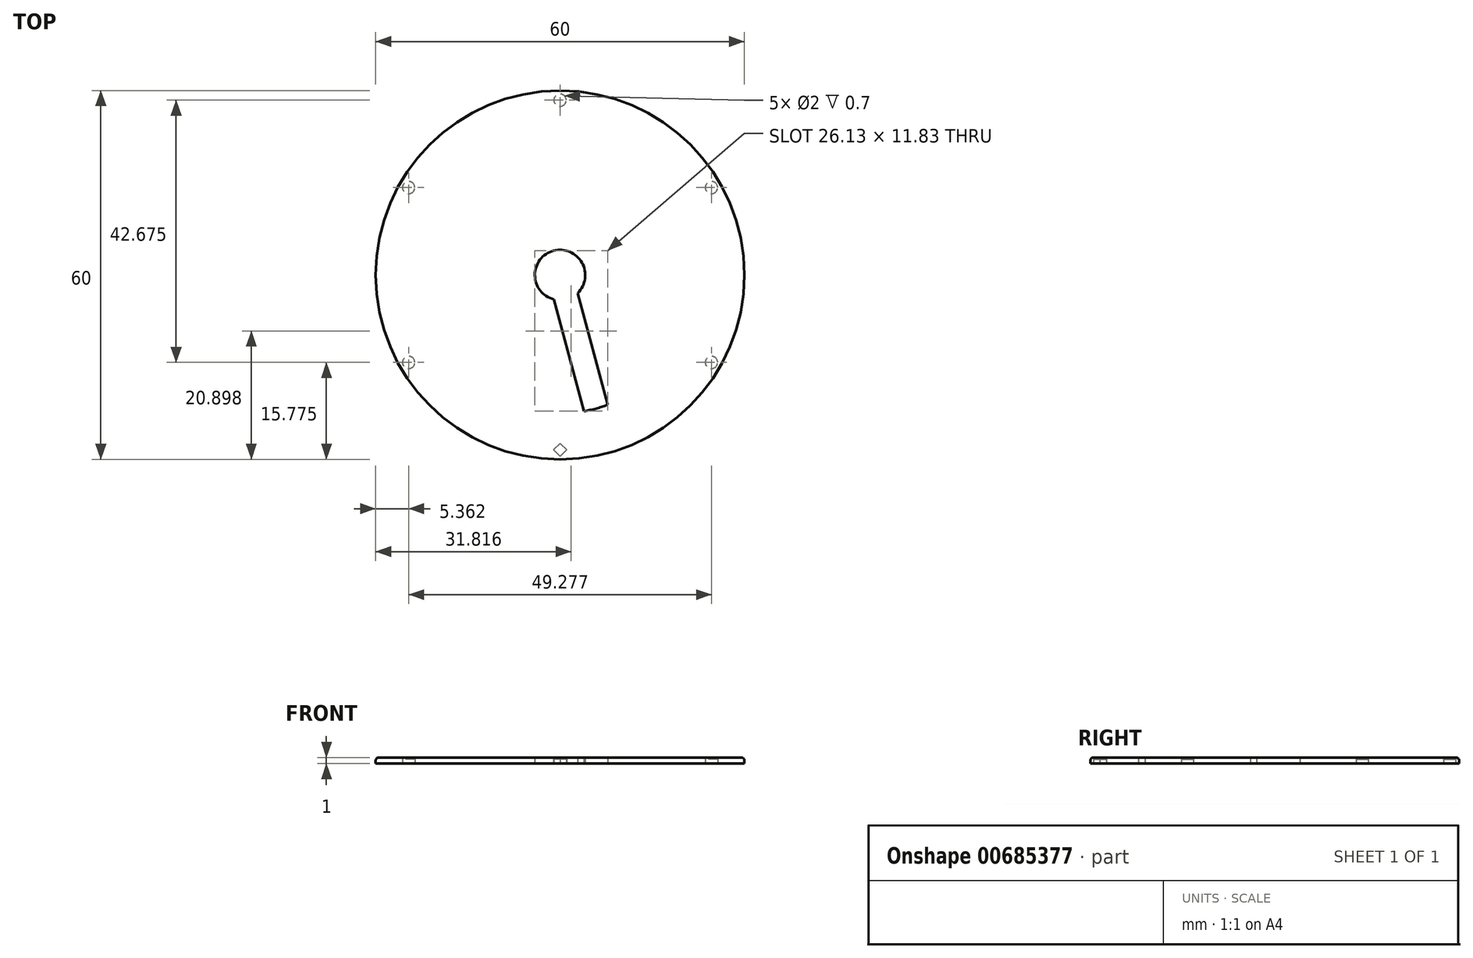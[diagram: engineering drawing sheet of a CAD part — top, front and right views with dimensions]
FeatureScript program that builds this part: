
annotation { "Feature Type Name" : "Feature", "Feature Type Description" : "" }
export const myFeature = defineFeature(function(context is Context, id is Id, definition is map)
    precondition{}
    {
        {
            var Q0;
            Q0=qCreatedBy(makeId("Top.planeOp"),FACE);
            var sketch = newSketch(context, id + "F0", { "sketchPlane" : qUnion([Q0])});
            skCircle(sketch, "E0", {"center": v(0, 0) * mm, "radius": 30 * mm});
            skCircle(sketch, "E1.0", {"center": v(0, 0) * mm, "radius": 29 * mm});
            skLineSegment(sketch, "E2.bottom", {"start": v(14.56, 26.23) * mm, "end": v(15.43, 25.73) * mm});
            skLineSegment(sketch, "E2.top", {"start": v(-15.43, -25.73) * mm, "end": v(-14.56, -26.23) * mm});
            skLineSegment(sketch, "E2.left", {"start": v(14.56, 26.23) * mm, "end": v(-15.43, -25.73) * mm});
            skLineSegment(sketch, "E2.right", {"start": v(15.43, 25.73) * mm, "end": v(-14.56, -26.23) * mm});
            skLineSegment(sketch, "E3.bottom", {"start": v(25.73, 15.43) * mm, "end": v(26.23, 14.56) * mm});
            skLineSegment(sketch, "E3.top", {"start": v(-26.23, -14.56) * mm, "end": v(-25.73, -15.43) * mm});
            skLineSegment(sketch, "E3.left", {"start": v(25.73, 15.43) * mm, "end": v(-26.23, -14.56) * mm});
            skLineSegment(sketch, "E3.right", {"start": v(26.23, 14.56) * mm, "end": v(-25.73, -15.43) * mm});
            skLineSegment(sketch, "E4", {"start": v(-38.35, 0) * mm, "end": v(39.17, 0) * mm, "construction": true});
            skLineSegment(sketch, "E5", {"start": v(0, 42.5) * mm, "end": v(0, -42.47) * mm, "construction": true});
            skLineSegment(sketch, "E6.bottom", {"start": v(-30, 0.5) * mm, "end": v(30, 0.5) * mm});
            skLineSegment(sketch, "E6.top", {"start": v(-30, -0.5) * mm, "end": v(30, -0.5) * mm});
            skLineSegment(sketch, "E6.left", {"start": v(-30, 0.5) * mm, "end": v(-30, -0.5) * mm});
            skLineSegment(sketch, "E6.right", {"start": v(30, 0.5) * mm, "end": v(30, -0.5) * mm});
            skLineSegment(sketch, "E7.bottom", {"start": v(-25.73, 15.43) * mm, "end": v(26.23, -14.56) * mm});
            skLineSegment(sketch, "E7.top", {"start": v(-26.23, 14.56) * mm, "end": v(25.73, -15.43) * mm});
            skLineSegment(sketch, "E7.left", {"start": v(-25.73, 15.43) * mm, "end": v(-26.23, 14.56) * mm});
            skLineSegment(sketch, "E7.right", {"start": v(26.23, -14.56) * mm, "end": v(25.73, -15.43) * mm});
            skLineSegment(sketch, "E8.bottom", {"start": v(-0.5, 30) * mm, "end": v(0.5, 30) * mm});
            skLineSegment(sketch, "E8.top", {"start": v(-0.5, -30) * mm, "end": v(0.5, -30) * mm});
            skLineSegment(sketch, "E8.left", {"start": v(-0.5, 30) * mm, "end": v(-0.5, -30) * mm});
            skLineSegment(sketch, "E8.right", {"start": v(0.5, 30) * mm, "end": v(0.5, -30) * mm});
            skLineSegment(sketch, "E9.bottom", {"start": v(-15.43, 25.73) * mm, "end": v(-14.56, 26.23) * mm});
            skLineSegment(sketch, "E9.top", {"start": v(14.56, -26.23) * mm, "end": v(15.43, -25.73) * mm});
            skLineSegment(sketch, "E9.left", {"start": v(-15.43, 25.73) * mm, "end": v(14.56, -26.23) * mm});
            skLineSegment(sketch, "E9.right", {"start": v(-14.56, 26.23) * mm, "end": v(15.43, -25.73) * mm});
            skCircle(sketch, "E10", {"center": v(0, 0) * mm, "radius": 13.47 * mm});
            skSolve(sketch);
        }
        {
            var Q0;
            Q0=qCreatedBy(makeId("Top.planeOp"),FACE);
            var sketch = newSketch(context, id + "F1", { "sketchPlane" : qUnion([Q0])});
            skCircle(sketch, "E11", {"center": v(0, 0) * mm, "radius": 30 * mm});
            skCircle(sketch, "E12", {"center": v(0, 0) * mm, "radius": 29 * mm});
            skSolve(sketch);
        }
        {
            var Q0;
            Q0=makeQuery(id+"F1.imprint","IMPRINT",FACE,{"disambiguationData":[TD([[makeQuery(id+"F1.imprint","IMPRINT",EDGE,{"derivedFrom":sQuery(id+"F1.wireOp",EDGE,"E11")}),1.0]])]});
            extrude(context, id + "F2", {"entities" : qUnion([Q0]), "depth" : 1 * mm, "offsetDistance" : 25 * mm});
        }
        {
            var Q0;
            Q0=makeQuery(id+"F1.imprint","IMPRINT",FACE,{"disambiguationData":[TD([[makeQuery(id+"F1.imprint","IMPRINT",EDGE,{"derivedFrom":sQuery(id+"F1.wireOp",EDGE,"E11")}),1.0]])]});
            var Q1;
            Q1=makeQuery(id+"F1.imprint","IMPRINT",FACE,{"disambiguationData":[TD([[makeQuery(id+"F1.imprint","IMPRINT",EDGE,{"derivedFrom":sQuery(id+"F1.wireOp",EDGE,"E12")}),1.0]])]});
            extrude(context, id + "F3", {"entities" : qUnion([Q0, Q1]), "operationType" : NewBodyOperationType.ADD, "depth" : 1 * mm, "offsetDistance" : 25 * mm});
        }
        {
            var Q0;
            Q0=qCreatedBy(makeId("Top.planeOp"),FACE);
            var sketch = newSketch(context, id + "F4", { "sketchPlane" : qUnion([Q0])});
            skCircle(sketch, "E13", {"center": v(0, 0) * mm, "radius": 28.45 * mm});
            skLineSegment(sketch, "E14", {"start": v(0, 28.45) * mm, "end": v(0, -28.45) * mm, "construction": true});
            skLineSegment(sketch, "E15", {"start": v(24.64, 14.22) * mm, "end": v(0, 0) * mm, "construction": true});
            skLineSegment(sketch, "E16", {"start": v(14.23, 24.64) * mm, "end": v(0, 0) * mm, "construction": true});
            skLineSegment(sketch, "E17", {"start": v(0, 0) * mm, "end": v(28.45, 0) * mm, "construction": true});
            skLineSegment(sketch, "E18", {"start": v(0, 0) * mm, "end": v(24.64, -14.22) * mm, "construction": true});
            skLineSegment(sketch, "E19", {"start": v(0, 0) * mm, "end": v(14.23, -24.64) * mm, "construction": true});
            skLineSegment(sketch, "E20", {"start": v(0, 0) * mm, "end": v(-14.23, 24.64) * mm, "construction": true});
            skLineSegment(sketch, "E21", {"start": v(0, 0) * mm, "end": v(-24.64, 14.22) * mm, "construction": true});
            skLineSegment(sketch, "E22", {"start": v(0, 0) * mm, "end": v(-28.45, 0) * mm, "construction": true});
            skLineSegment(sketch, "E23", {"start": v(0, 0) * mm, "end": v(-24.64, -14.23) * mm, "construction": true});
            skLineSegment(sketch, "E24", {"start": v(0, 0) * mm, "end": v(-14.22, -24.64) * mm, "construction": true});
            skCircle(sketch, "E25", {"center": v(0, 28.45) * mm, "radius": 1.5 * mm});
            skCircle(sketch, "E26", {"center": v(24.64, 14.22) * mm, "radius": 1.5 * mm});
            skCircle(sketch, "E27", {"center": v(24.64, -14.22) * mm, "radius": 1.5 * mm});
            skCircle(sketch, "E28", {"center": v(0, -28.45) * mm, "radius": 1.5 * mm});
            skCircle(sketch, "E29", {"center": v(-24.64, -14.23) * mm, "radius": 1.5 * mm});
            skCircle(sketch, "E30", {"center": v(-24.64, 14.22) * mm, "radius": 1.5 * mm});
            skCircle(sketch, "E31", {"center": v(-24.64, 14.22) * mm, "radius": 1 * mm});
            skCircle(sketch, "E32", {"center": v(0, 28.45) * mm, "radius": 1 * mm});
            skCircle(sketch, "E33", {"center": v(24.64, 14.22) * mm, "radius": 1 * mm});
            skCircle(sketch, "E34", {"center": v(24.64, -14.22) * mm, "radius": 1 * mm});
            skCircle(sketch, "E35", {"center": v(-24.64, -14.23) * mm, "radius": 1 * mm});
            skLineSegment(sketch, "E36.bottom", {"start": v(1.06, -28.45) * mm, "end": v(0, -29.51) * mm});
            skLineSegment(sketch, "E36.top", {"start": v(0, -27.39) * mm, "end": v(-1.06, -28.45) * mm});
            skLineSegment(sketch, "E36.left", {"start": v(1.06, -28.45) * mm, "end": v(0, -27.39) * mm});
            skLineSegment(sketch, "E36.right", {"start": v(0, -29.51) * mm, "end": v(-1.06, -28.45) * mm});
            skSolve(sketch);
        }
        {
            var Q0;
            {var subQ0=sQuery(id+"F4.wireOp",EDGE,"E30");var subQ1=sQuery(id+"F4.wireOp",EDGE,"E13");var subQ2=makeQuery(id+"F4.imprint","INTERSECT",VERTEX,{"disambiguationData":[OD(0.0)],"derivedFrom":[subQ1,subQ0]});Q0=makeQuery(id+"F4.imprint","IMPRINT",FACE,{"disambiguationData":[TD([[makeQuery(id+"F4.imprint","IMPRINT",EDGE,{"disambiguationData":[TD([[subQ2,-1.0]])],"derivedFrom":subQ1}),1.0]])]});}
            var Q1;
            {var subQ0=sQuery(id+"F4.wireOp",EDGE,"E30");var subQ1=sQuery(id+"F4.wireOp",EDGE,"E13");var subQ2=makeQuery(id+"F4.imprint","INTERSECT",VERTEX,{"disambiguationData":[OD(0.0)],"derivedFrom":[subQ1,subQ0]});Q1=makeQuery(id+"F4.imprint","IMPRINT",FACE,{"disambiguationData":[TD([[makeQuery(id+"F4.imprint","IMPRINT",EDGE,{"disambiguationData":[TD([[subQ2,-1.0]])],"derivedFrom":subQ1}),-1.0]])]});}
            var Q2;
            {var subQ0=sQuery(id+"F4.wireOp",EDGE,"E25");var subQ1=sQuery(id+"F4.wireOp",EDGE,"E13");var subQ2=makeQuery(id+"F4.imprint","INTERSECT",VERTEX,{"disambiguationData":[OD(0.0)],"derivedFrom":[subQ1,subQ0]});Q2=makeQuery(id+"F4.imprint","IMPRINT",FACE,{"disambiguationData":[TD([[makeQuery(id+"F4.imprint","IMPRINT",EDGE,{"disambiguationData":[TD([[subQ2,-1.0]])],"derivedFrom":subQ1}),1.0]])]});}
            var Q3;
            {var subQ0=sQuery(id+"F4.wireOp",EDGE,"E25");var subQ1=sQuery(id+"F4.wireOp",EDGE,"E13");var subQ2=makeQuery(id+"F4.imprint","INTERSECT",VERTEX,{"disambiguationData":[OD(0.0)],"derivedFrom":[subQ1,subQ0]});Q3=makeQuery(id+"F4.imprint","IMPRINT",FACE,{"disambiguationData":[TD([[makeQuery(id+"F4.imprint","IMPRINT",EDGE,{"disambiguationData":[TD([[subQ2,-1.0]])],"derivedFrom":subQ1}),-1.0]])]});}
            var Q4;
            {var subQ0=sQuery(id+"F4.wireOp",EDGE,"E26");var subQ1=sQuery(id+"F4.wireOp",EDGE,"E13");var subQ2=makeQuery(id+"F4.imprint","INTERSECT",VERTEX,{"disambiguationData":[OD(0.0)],"derivedFrom":[subQ1,subQ0]});Q4=makeQuery(id+"F4.imprint","IMPRINT",FACE,{"disambiguationData":[TD([[makeQuery(id+"F4.imprint","IMPRINT",EDGE,{"disambiguationData":[TD([[subQ2,-1.0]])],"derivedFrom":subQ1}),-1.0]])]});}
            var Q5;
            {var subQ0=sQuery(id+"F4.wireOp",EDGE,"E26");var subQ1=sQuery(id+"F4.wireOp",EDGE,"E13");var subQ2=makeQuery(id+"F4.imprint","INTERSECT",VERTEX,{"disambiguationData":[OD(0.0)],"derivedFrom":[subQ1,subQ0]});Q5=makeQuery(id+"F4.imprint","IMPRINT",FACE,{"disambiguationData":[TD([[makeQuery(id+"F4.imprint","IMPRINT",EDGE,{"disambiguationData":[TD([[subQ2,-1.0]])],"derivedFrom":subQ1}),1.0]])]});}
            var Q6;
            {var subQ0=sQuery(id+"F4.wireOp",EDGE,"E29");var subQ1=sQuery(id+"F4.wireOp",EDGE,"E13");var subQ2=makeQuery(id+"F4.imprint","INTERSECT",VERTEX,{"disambiguationData":[OD(0.0)],"derivedFrom":[subQ1,subQ0]});Q6=makeQuery(id+"F4.imprint","IMPRINT",FACE,{"disambiguationData":[TD([[makeQuery(id+"F4.imprint","IMPRINT",EDGE,{"disambiguationData":[TD([[subQ2,-1.0]])],"derivedFrom":subQ1}),1.0]])]});}
            var Q7;
            {var subQ0=sQuery(id+"F4.wireOp",EDGE,"E29");var subQ1=sQuery(id+"F4.wireOp",EDGE,"E13");var subQ2=makeQuery(id+"F4.imprint","INTERSECT",VERTEX,{"disambiguationData":[OD(0.0)],"derivedFrom":[subQ1,subQ0]});Q7=makeQuery(id+"F4.imprint","IMPRINT",FACE,{"disambiguationData":[TD([[makeQuery(id+"F4.imprint","IMPRINT",EDGE,{"disambiguationData":[TD([[subQ2,-1.0]])],"derivedFrom":subQ1}),-1.0]])]});}
            var Q8;
            {var subQ3=sQuery(id+"F4.wireOp",EDGE,"E13");var subQ5=sQuery(id+"F4.wireOp",EDGE,"E28");var subQ6=makeQuery(id+"F4.imprint","INTERSECT",VERTEX,{"disambiguationData":[OD(0.0)],"derivedFrom":[subQ3,subQ5]});Q8=makeQuery(id+"F4.imprint","IMPRINT",FACE,{"disambiguationData":[TD([[makeQuery(id+"F4.imprint","IMPRINT",EDGE,{"disambiguationData":[TD([[subQ6,-1.0]])],"derivedFrom":subQ3}),1.0]])]});}
            var Q9;
            {var subQ6=sQuery(id+"F4.wireOp",EDGE,"E36.bottom");Q9=makeQuery(id+"F4.imprint","IMPRINT",FACE,{"disambiguationData":[TD([[makeQuery(id+"F4.imprint","IMPRINT",EDGE,{"derivedFrom":subQ6}),1.0]])]});}
            var Q10;
            {var subQ0=sQuery(id+"F4.wireOp",EDGE,"E27");var subQ1=sQuery(id+"F4.wireOp",EDGE,"E13");var subQ2=makeQuery(id+"F4.imprint","INTERSECT",VERTEX,{"disambiguationData":[OD(0.0)],"derivedFrom":[subQ1,subQ0]});Q10=makeQuery(id+"F4.imprint","IMPRINT",FACE,{"disambiguationData":[TD([[makeQuery(id+"F4.imprint","IMPRINT",EDGE,{"disambiguationData":[TD([[subQ2,-1.0]])],"derivedFrom":subQ1}),-1.0]])]});}
            var Q11;
            {var subQ0=sQuery(id+"F4.wireOp",EDGE,"E27");var subQ1=sQuery(id+"F4.wireOp",EDGE,"E13");var subQ2=makeQuery(id+"F4.imprint","INTERSECT",VERTEX,{"disambiguationData":[OD(0.0)],"derivedFrom":[subQ1,subQ0]});Q11=makeQuery(id+"F4.imprint","IMPRINT",FACE,{"disambiguationData":[TD([[makeQuery(id+"F4.imprint","IMPRINT",EDGE,{"disambiguationData":[TD([[subQ2,-1.0]])],"derivedFrom":subQ1}),1.0]])]});}
            var Q12;
            {var subQ0=sQuery(id+"F4.wireOp",EDGE,"E31");var subQ1=sQuery(id+"F4.wireOp",EDGE,"E13");var subQ2=makeQuery(id+"F4.imprint","INTERSECT",VERTEX,{"disambiguationData":[OD(0.0)],"derivedFrom":[subQ1,subQ0]});Q12=makeQuery(id+"F4.imprint","IMPRINT",FACE,{"disambiguationData":[TD([[makeQuery(id+"F4.imprint","IMPRINT",EDGE,{"disambiguationData":[TD([[subQ2,-1.0]])],"derivedFrom":subQ1}),1.0]])]});}
            var Q13;
            {var subQ0=sQuery(id+"F4.wireOp",EDGE,"E31");var subQ1=sQuery(id+"F4.wireOp",EDGE,"E13");var subQ2=makeQuery(id+"F4.imprint","INTERSECT",VERTEX,{"disambiguationData":[OD(0.0)],"derivedFrom":[subQ1,subQ0]});Q13=makeQuery(id+"F4.imprint","IMPRINT",FACE,{"disambiguationData":[TD([[makeQuery(id+"F4.imprint","IMPRINT",EDGE,{"disambiguationData":[TD([[subQ2,-1.0]])],"derivedFrom":subQ1}),-1.0]])]});}
            var Q14;
            {var subQ0=sQuery(id+"F4.wireOp",EDGE,"E32");var subQ1=sQuery(id+"F4.wireOp",EDGE,"E13");var subQ2=makeQuery(id+"F4.imprint","INTERSECT",VERTEX,{"disambiguationData":[OD(0.0)],"derivedFrom":[subQ1,subQ0]});Q14=makeQuery(id+"F4.imprint","IMPRINT",FACE,{"disambiguationData":[TD([[makeQuery(id+"F4.imprint","IMPRINT",EDGE,{"disambiguationData":[TD([[subQ2,-1.0]])],"derivedFrom":subQ1}),-1.0]])]});}
            var Q15;
            {var subQ0=sQuery(id+"F4.wireOp",EDGE,"E32");var subQ1=sQuery(id+"F4.wireOp",EDGE,"E13");var subQ2=makeQuery(id+"F4.imprint","INTERSECT",VERTEX,{"disambiguationData":[OD(0.0)],"derivedFrom":[subQ1,subQ0]});Q15=makeQuery(id+"F4.imprint","IMPRINT",FACE,{"disambiguationData":[TD([[makeQuery(id+"F4.imprint","IMPRINT",EDGE,{"disambiguationData":[TD([[subQ2,-1.0]])],"derivedFrom":subQ1}),1.0]])]});}
            var Q16;
            {var subQ0=sQuery(id+"F4.wireOp",EDGE,"E33");var subQ1=sQuery(id+"F4.wireOp",EDGE,"E13");var subQ2=makeQuery(id+"F4.imprint","INTERSECT",VERTEX,{"disambiguationData":[OD(0.0)],"derivedFrom":[subQ1,subQ0]});Q16=makeQuery(id+"F4.imprint","IMPRINT",FACE,{"disambiguationData":[TD([[makeQuery(id+"F4.imprint","IMPRINT",EDGE,{"disambiguationData":[TD([[subQ2,-1.0]])],"derivedFrom":subQ1}),-1.0]])]});}
            var Q17;
            {var subQ0=sQuery(id+"F4.wireOp",EDGE,"E33");var subQ1=sQuery(id+"F4.wireOp",EDGE,"E13");var subQ2=makeQuery(id+"F4.imprint","INTERSECT",VERTEX,{"disambiguationData":[OD(0.0)],"derivedFrom":[subQ1,subQ0]});Q17=makeQuery(id+"F4.imprint","IMPRINT",FACE,{"disambiguationData":[TD([[makeQuery(id+"F4.imprint","IMPRINT",EDGE,{"disambiguationData":[TD([[subQ2,-1.0]])],"derivedFrom":subQ1}),1.0]])]});}
            var Q18;
            {var subQ0=sQuery(id+"F4.wireOp",EDGE,"E34");var subQ1=sQuery(id+"F4.wireOp",EDGE,"E13");var subQ2=makeQuery(id+"F4.imprint","INTERSECT",VERTEX,{"disambiguationData":[OD(0.0)],"derivedFrom":[subQ1,subQ0]});Q18=makeQuery(id+"F4.imprint","IMPRINT",FACE,{"disambiguationData":[TD([[makeQuery(id+"F4.imprint","IMPRINT",EDGE,{"disambiguationData":[TD([[subQ2,-1.0]])],"derivedFrom":subQ1}),-1.0]])]});}
            var Q19;
            {var subQ0=sQuery(id+"F4.wireOp",EDGE,"E34");var subQ1=sQuery(id+"F4.wireOp",EDGE,"E13");var subQ2=makeQuery(id+"F4.imprint","INTERSECT",VERTEX,{"disambiguationData":[OD(0.0)],"derivedFrom":[subQ1,subQ0]});Q19=makeQuery(id+"F4.imprint","IMPRINT",FACE,{"disambiguationData":[TD([[makeQuery(id+"F4.imprint","IMPRINT",EDGE,{"disambiguationData":[TD([[subQ2,-1.0]])],"derivedFrom":subQ1}),1.0]])]});}
            var Q20;
            {var subQ1=sQuery(id+"F4.wireOp",EDGE,"E36.bottom");Q20=makeQuery(id+"F4.imprint","IMPRINT",FACE,{"disambiguationData":[TD([[makeQuery(id+"F4.imprint","IMPRINT",EDGE,{"derivedFrom":subQ1}),-1.0]])]});}
            var Q21;
            {var subQ0=sQuery(id+"F4.wireOp",EDGE,"E35");var subQ1=sQuery(id+"F4.wireOp",EDGE,"E13");var subQ2=makeQuery(id+"F4.imprint","INTERSECT",VERTEX,{"disambiguationData":[OD(0.0)],"derivedFrom":[subQ1,subQ0]});Q21=makeQuery(id+"F4.imprint","IMPRINT",FACE,{"disambiguationData":[TD([[makeQuery(id+"F4.imprint","IMPRINT",EDGE,{"disambiguationData":[TD([[subQ2,-1.0]])],"derivedFrom":subQ1}),-1.0]])]});}
            var Q22;
            {var subQ0=sQuery(id+"F4.wireOp",EDGE,"E35");var subQ1=sQuery(id+"F4.wireOp",EDGE,"E13");var subQ2=makeQuery(id+"F4.imprint","INTERSECT",VERTEX,{"disambiguationData":[OD(0.0)],"derivedFrom":[subQ1,subQ0]});Q22=makeQuery(id+"F4.imprint","IMPRINT",FACE,{"disambiguationData":[TD([[makeQuery(id+"F4.imprint","IMPRINT",EDGE,{"disambiguationData":[TD([[subQ2,-1.0]])],"derivedFrom":subQ1}),1.0]])]});}
            var Q23;
            {var subQ0=sQuery(id+"F4.wireOp",EDGE,"E36.top");var subQ1=sQuery(id+"F4.wireOp",EDGE,"E13");var subQ2=makeQuery(id+"F4.imprint","INTERSECT",VERTEX,{"derivedFrom":[subQ1,subQ0]});Q23=makeQuery(id+"F4.imprint","IMPRINT",FACE,{"disambiguationData":[TD([[makeQuery(id+"F4.imprint","IMPRINT",EDGE,{"disambiguationData":[TD([[subQ2,-1.0]])],"derivedFrom":subQ1}),1.0]])]});}
            extrude(context, id + "F5", {"entities" : qUnion([Q0, Q1, Q2, Q3, Q4, Q5, Q6, Q7, Q8, Q9, Q10, Q11, Q12, Q13, Q14, Q15, Q16, Q17, Q18, Q19, Q20, Q21, Q22, Q23]), "operationType" : NewBodyOperationType.ADD, "depth" : 1 * mm, "offsetDistance" : 25 * mm});
        }
        {
            var Q0;
            {var subQ0=sQuery(id+"F4.wireOp",EDGE,"E31");var subQ1=sQuery(id+"F4.wireOp",EDGE,"E13");var subQ2=makeQuery(id+"F4.imprint","INTERSECT",VERTEX,{"disambiguationData":[OD(0.0)],"derivedFrom":[subQ1,subQ0]});Q0=makeQuery(id+"F4.imprint","IMPRINT",FACE,{"disambiguationData":[TD([[makeQuery(id+"F4.imprint","IMPRINT",EDGE,{"disambiguationData":[TD([[subQ2,-1.0]])],"derivedFrom":subQ1}),-1.0]])]});}
            var Q1;
            {var subQ0=sQuery(id+"F4.wireOp",EDGE,"E31");var subQ1=sQuery(id+"F4.wireOp",EDGE,"E13");var subQ2=makeQuery(id+"F4.imprint","INTERSECT",VERTEX,{"disambiguationData":[OD(0.0)],"derivedFrom":[subQ1,subQ0]});Q1=makeQuery(id+"F4.imprint","IMPRINT",FACE,{"disambiguationData":[TD([[makeQuery(id+"F4.imprint","IMPRINT",EDGE,{"disambiguationData":[TD([[subQ2,-1.0]])],"derivedFrom":subQ1}),1.0]])]});}
            var Q2;
            {var subQ0=sQuery(id+"F4.wireOp",EDGE,"E32");var subQ1=sQuery(id+"F4.wireOp",EDGE,"E13");var subQ2=makeQuery(id+"F4.imprint","INTERSECT",VERTEX,{"disambiguationData":[OD(0.0)],"derivedFrom":[subQ1,subQ0]});Q2=makeQuery(id+"F4.imprint","IMPRINT",FACE,{"disambiguationData":[TD([[makeQuery(id+"F4.imprint","IMPRINT",EDGE,{"disambiguationData":[TD([[subQ2,-1.0]])],"derivedFrom":subQ1}),-1.0]])]});}
            var Q3;
            {var subQ0=sQuery(id+"F4.wireOp",EDGE,"E32");var subQ1=sQuery(id+"F4.wireOp",EDGE,"E13");var subQ2=makeQuery(id+"F4.imprint","INTERSECT",VERTEX,{"disambiguationData":[OD(0.0)],"derivedFrom":[subQ1,subQ0]});Q3=makeQuery(id+"F4.imprint","IMPRINT",FACE,{"disambiguationData":[TD([[makeQuery(id+"F4.imprint","IMPRINT",EDGE,{"disambiguationData":[TD([[subQ2,-1.0]])],"derivedFrom":subQ1}),1.0]])]});}
            var Q4;
            {var subQ0=sQuery(id+"F4.wireOp",EDGE,"E33");var subQ1=sQuery(id+"F4.wireOp",EDGE,"E13");var subQ2=makeQuery(id+"F4.imprint","INTERSECT",VERTEX,{"disambiguationData":[OD(0.0)],"derivedFrom":[subQ1,subQ0]});Q4=makeQuery(id+"F4.imprint","IMPRINT",FACE,{"disambiguationData":[TD([[makeQuery(id+"F4.imprint","IMPRINT",EDGE,{"disambiguationData":[TD([[subQ2,-1.0]])],"derivedFrom":subQ1}),1.0]])]});}
            var Q5;
            {var subQ0=sQuery(id+"F4.wireOp",EDGE,"E33");var subQ1=sQuery(id+"F4.wireOp",EDGE,"E13");var subQ2=makeQuery(id+"F4.imprint","INTERSECT",VERTEX,{"disambiguationData":[OD(0.0)],"derivedFrom":[subQ1,subQ0]});Q5=makeQuery(id+"F4.imprint","IMPRINT",FACE,{"disambiguationData":[TD([[makeQuery(id+"F4.imprint","IMPRINT",EDGE,{"disambiguationData":[TD([[subQ2,-1.0]])],"derivedFrom":subQ1}),-1.0]])]});}
            var Q6;
            {var subQ0=sQuery(id+"F4.wireOp",EDGE,"E34");var subQ1=sQuery(id+"F4.wireOp",EDGE,"E13");var subQ2=makeQuery(id+"F4.imprint","INTERSECT",VERTEX,{"disambiguationData":[OD(0.0)],"derivedFrom":[subQ1,subQ0]});Q6=makeQuery(id+"F4.imprint","IMPRINT",FACE,{"disambiguationData":[TD([[makeQuery(id+"F4.imprint","IMPRINT",EDGE,{"disambiguationData":[TD([[subQ2,-1.0]])],"derivedFrom":subQ1}),1.0]])]});}
            var Q7;
            {var subQ0=sQuery(id+"F4.wireOp",EDGE,"E34");var subQ1=sQuery(id+"F4.wireOp",EDGE,"E13");var subQ2=makeQuery(id+"F4.imprint","INTERSECT",VERTEX,{"disambiguationData":[OD(0.0)],"derivedFrom":[subQ1,subQ0]});Q7=makeQuery(id+"F4.imprint","IMPRINT",FACE,{"disambiguationData":[TD([[makeQuery(id+"F4.imprint","IMPRINT",EDGE,{"disambiguationData":[TD([[subQ2,-1.0]])],"derivedFrom":subQ1}),-1.0]])]});}
            var Q8;
            {var subQ1=sQuery(id+"F4.wireOp",EDGE,"E36.bottom");Q8=makeQuery(id+"F4.imprint","IMPRINT",FACE,{"disambiguationData":[TD([[makeQuery(id+"F4.imprint","IMPRINT",EDGE,{"derivedFrom":subQ1}),-1.0]])]});}
            var Q9;
            {var subQ0=sQuery(id+"F4.wireOp",EDGE,"E36.top");var subQ1=sQuery(id+"F4.wireOp",EDGE,"E13");var subQ2=makeQuery(id+"F4.imprint","INTERSECT",VERTEX,{"derivedFrom":[subQ1,subQ0]});Q9=makeQuery(id+"F4.imprint","IMPRINT",FACE,{"disambiguationData":[TD([[makeQuery(id+"F4.imprint","IMPRINT",EDGE,{"disambiguationData":[TD([[subQ2,-1.0]])],"derivedFrom":subQ1}),1.0]])]});}
            var Q10;
            {var subQ0=sQuery(id+"F4.wireOp",EDGE,"E35");var subQ1=sQuery(id+"F4.wireOp",EDGE,"E13");var subQ2=makeQuery(id+"F4.imprint","INTERSECT",VERTEX,{"disambiguationData":[OD(0.0)],"derivedFrom":[subQ1,subQ0]});Q10=makeQuery(id+"F4.imprint","IMPRINT",FACE,{"disambiguationData":[TD([[makeQuery(id+"F4.imprint","IMPRINT",EDGE,{"disambiguationData":[TD([[subQ2,-1.0]])],"derivedFrom":subQ1}),-1.0]])]});}
            var Q11;
            {var subQ0=sQuery(id+"F4.wireOp",EDGE,"E35");var subQ1=sQuery(id+"F4.wireOp",EDGE,"E13");var subQ2=makeQuery(id+"F4.imprint","INTERSECT",VERTEX,{"disambiguationData":[OD(0.0)],"derivedFrom":[subQ1,subQ0]});Q11=makeQuery(id+"F4.imprint","IMPRINT",FACE,{"disambiguationData":[TD([[makeQuery(id+"F4.imprint","IMPRINT",EDGE,{"disambiguationData":[TD([[subQ2,-1.0]])],"derivedFrom":subQ1}),1.0]])]});}
            extrude(context, id + "F6", {"entities" : qUnion([Q0, Q1, Q2, Q3, Q4, Q5, Q6, Q7, Q8, Q9, Q10, Q11]), "operationType" : NewBodyOperationType.REMOVE, "depth" : .7 * mm, "offsetDistance" : 25 * mm});
        }
        {
            var Q0;
            Q0=qCreatedBy(makeId("Top.planeOp"),FACE);
            var sketch = newSketch(context, id + "F7", { "sketchPlane" : qUnion([Q0])});
            skCircle(sketch, "E37", {"center": v(0, 0) * mm, "radius": 4.1 * mm});
            skLineSegment(sketch, "E38", {"start": v(0, 0) * mm, "end": v(7.76, -28.98) * mm});
            skLineSegment(sketch, "E39.0", {"start": v(-1.93, -0.52) * mm, "end": v(5.91, -29.8) * mm});
            skLineSegment(sketch, "E40.0", {"start": v(1.93, 0.52) * mm, "end": v(9.8, -28.83) * mm});
            skCircle(sketch, "E41", {"center": v(0, 0) * mm, "radius": 22.5 * mm});
            skSolve(sketch);
        }
        {
            var Q0;
            {var subQ0=sQuery(id+"F7.wireOp",EDGE,"E37");var subQ1=makeQuery(id+"F7.imprint","INTERSECT",VERTEX,{"derivedFrom":[subQ0,sQuery(id+"F7.wireOp",EDGE,"E39.0")]});Q0=makeQuery(id+"F7.imprint","IMPRINT",FACE,{"disambiguationData":[TD([[makeQuery(id+"F7.imprint","IMPRINT",EDGE,{"disambiguationData":[TD([[subQ1,-1.0]])],"derivedFrom":subQ0}),1.0]])]});}
            var Q1;
            {var subQ0=sQuery(id+"F7.wireOp",EDGE,"E39.0");var subQ1=sQuery(id+"F7.wireOp",EDGE,"E37");var subQ2=makeQuery(id+"F7.imprint","INTERSECT",VERTEX,{"derivedFrom":[subQ1,subQ0]});Q1=makeQuery(id+"F7.imprint","IMPRINT",FACE,{"disambiguationData":[TD([[makeQuery(id+"F7.imprint","IMPRINT",EDGE,{"disambiguationData":[TD([[subQ2,-1.0]])],"derivedFrom":subQ1}),-1.0]])]});}
            var Q2;
            {var subQ0=sQuery(id+"F7.wireOp",EDGE,"E40.0");var subQ1=sQuery(id+"F7.wireOp",EDGE,"E37");var subQ2=makeQuery(id+"F7.imprint","INTERSECT",VERTEX,{"derivedFrom":[subQ1,subQ0]});Q2=makeQuery(id+"F7.imprint","IMPRINT",FACE,{"disambiguationData":[TD([[makeQuery(id+"F7.imprint","IMPRINT",EDGE,{"disambiguationData":[TD([[subQ2,1.0]])],"derivedFrom":subQ1}),-1.0]])]});}
            var Q3;
            {var subQ0=sQuery(id+"F7.wireOp",EDGE,"hZQpLc18-hGwi-RvbU-mkqQ-O1lpG7E0jyzC");var subQ1=sQuery(id+"F7.wireOp",EDGE,"E38");var subQ2=makeQuery(id+"F7.imprint","INTERSECT",VERTEX,{"disambiguationData":[OD(0.0)],"derivedFrom":[subQ1,subQ0]});Q3=makeQuery(id+"F7.imprint","IMPRINT",FACE,{"disambiguationData":[TD([[makeQuery(id+"F7.imprint","IMPRINT",EDGE,{"disambiguationData":[TD([[subQ2,1.0]])],"derivedFrom":subQ1}),1.0]])]});}
            var Q4;
            {var subQ0=sQuery(id+"F7.wireOp",EDGE,"hZQpLc18-hGwi-RvbU-mkqQ-O1lpG7E0jyzC");var subQ1=sQuery(id+"F7.wireOp",EDGE,"E38");var subQ2=makeQuery(id+"F7.imprint","INTERSECT",VERTEX,{"disambiguationData":[OD(0.0)],"derivedFrom":[subQ1,subQ0]});Q4=makeQuery(id+"F7.imprint","IMPRINT",FACE,{"disambiguationData":[TD([[makeQuery(id+"F7.imprint","IMPRINT",EDGE,{"disambiguationData":[TD([[subQ2,1.0]])],"derivedFrom":subQ1}),-1.0]])]});}
            extrude(context, id + "F8", {"entities" : qUnion([Q0, Q1, Q2, Q3, Q4]), "operationType" : NewBodyOperationType.REMOVE, "depth" : 1 * mm, "offsetDistance" : 25 * mm});
        }
        {
            var Q0;
            {var subQ0=sQuery(id+"F4.wireOp",EDGE,"E28");var subQ1=sQuery(id+"F4.wireOp",EDGE,"E27");var subQ2=sQuery(id+"F1.wireOp",EDGE,"E11");Q0=makeQuery(id+"F5.boolean.opBoolean","SPLIT",EDGE,{"disambiguationData":[TD([makeQuery(id+"F2.opExtrude","SWEPT_FACE",FACE,{"disambiguationData":[OSD([subQ2])]}),makeQuery(id+"F2.opExtrude","CAP_FACE",FACE,{"disambiguationData":[OSD([subQ2,sQuery(id+"F1.wireOp",EDGE,"E12")])],"isStart":false}),makeQuery(id+"F3.opExtrude","CAP_FACE",FACE,{"disambiguationData":[OSD([subQ2])],"isStart":false}),makeQuery(id+"F5.opExtrude","CAP_FACE",FACE,{"disambiguationData":[OSD([sQuery(id+"F4.wireOp",EDGE,"E25")])],"isStart":false}),makeQuery(id+"F5.opExtrude","CAP_FACE",FACE,{"disambiguationData":[OSD([sQuery(id+"F4.wireOp",EDGE,"E26")])],"isStart":false}),makeQuery(id+"F5.opExtrude","SWEPT_FACE",FACE,{"disambiguationData":[OSD([subQ1])]}),makeQuery(id+"F5.opExtrude","CAP_FACE",FACE,{"disambiguationData":[OSD([subQ1])],"isStart":false}),makeQuery(id+"F5.opExtrude","SWEPT_FACE",FACE,{"disambiguationData":[OSD([subQ0])]}),makeQuery(id+"F5.opExtrude","CAP_FACE",FACE,{"disambiguationData":[OSD([subQ0])],"isStart":false}),makeQuery(id+"F5.opExtrude","CAP_FACE",FACE,{"disambiguationData":[OSD([sQuery(id+"F4.wireOp",EDGE,"E29")])],"isStart":false}),makeQuery(id+"F5.opExtrude","CAP_FACE",FACE,{"disambiguationData":[OSD([sQuery(id+"F4.wireOp",EDGE,"E30")])],"isStart":false})])],"derivedFrom":makeQuery(id+"F2.opExtrude","CAP_EDGE",EDGE,{"disambiguationData":[OSD([subQ2])],"isStart":false})});}
            var Q1;
            Q1=makeQuery(id+"F8.boolean.opBoolean","COPY",EDGE,{"derivedFrom":makeQuery(id+"F8.opExtrude","CAP_EDGE",EDGE,{"disambiguationData":[OSD([sQuery(id+"F7.wireOp",EDGE,"E37")])],"isStart":false})});
            var Q2;
            Q2=makeQuery(id+"F8.boolean.opBoolean","COPY",EDGE,{"derivedFrom":makeQuery(id+"F8.opExtrude","CAP_EDGE",EDGE,{"disambiguationData":[OSD([sQuery(id+"F7.wireOp",EDGE,"E39.0")])],"isStart":false})});
            var Q3;
            Q3=makeQuery(id+"F8.boolean.opBoolean","COPY",EDGE,{"derivedFrom":makeQuery(id+"F8.opExtrude","CAP_EDGE",EDGE,{"disambiguationData":[OSD([sQuery(id+"F7.wireOp",EDGE,"hZQpLc18-hGwi-RvbU-mkqQ-O1lpG7E0jyzC")])],"isStart":false})});
            var Q4;
            Q4=makeQuery(id+"F8.boolean.opBoolean","COPY",EDGE,{"derivedFrom":makeQuery(id+"F8.opExtrude","CAP_EDGE",EDGE,{"disambiguationData":[OSD([sQuery(id+"F7.wireOp",EDGE,"E40.0")])],"isStart":false})});
            var Q5;
            Q5=makeQuery(id+"F8.boolean.opBoolean","COPY",EDGE,{"derivedFrom":makeQuery(id+"F8.opExtrude","CAP_EDGE",EDGE,{"disambiguationData":[OSD([sQuery(id+"F7.wireOp",EDGE,"E40.0")])],"isStart":true})});
            var Q6;
            Q6=makeQuery(id+"F8.boolean.opBoolean","COPY",EDGE,{"derivedFrom":makeQuery(id+"F8.opExtrude","CAP_EDGE",EDGE,{"disambiguationData":[OSD([sQuery(id+"F7.wireOp",EDGE,"E37")])],"isStart":true})});
            var Q7;
            Q7=makeQuery(id+"F8.boolean.opBoolean","COPY",EDGE,{"derivedFrom":makeQuery(id+"F8.opExtrude","CAP_EDGE",EDGE,{"disambiguationData":[OSD([sQuery(id+"F7.wireOp",EDGE,"E39.0")])],"isStart":true})});
            var Q8;
            Q8=makeQuery(id+"F8.boolean.opBoolean","COPY",EDGE,{"derivedFrom":makeQuery(id+"F8.opExtrude","CAP_EDGE",EDGE,{"disambiguationData":[OSD([sQuery(id+"F7.wireOp",EDGE,"hZQpLc18-hGwi-RvbU-mkqQ-O1lpG7E0jyzC")])],"isStart":true})});
            var Q9;
            Q9=makeQuery(id+"F8.boolean.opBoolean","COPY",EDGE,{"derivedFrom":makeQuery(id+"F8.opExtrude","CAP_EDGE",EDGE,{"disambiguationData":[OSD([sQuery(id+"F7.wireOp",EDGE,"E41")])],"isStart":false})});
            fillet(context, id + "F9", {"entities" : qUnion([Q0, Q1, Q2, Q3, Q4, Q5, Q6, Q7, Q8, Q9]), "radius" : .5 * mm, "tangentPropagation" : true, "allowEdgeOverflow" : false});
        }
    });
